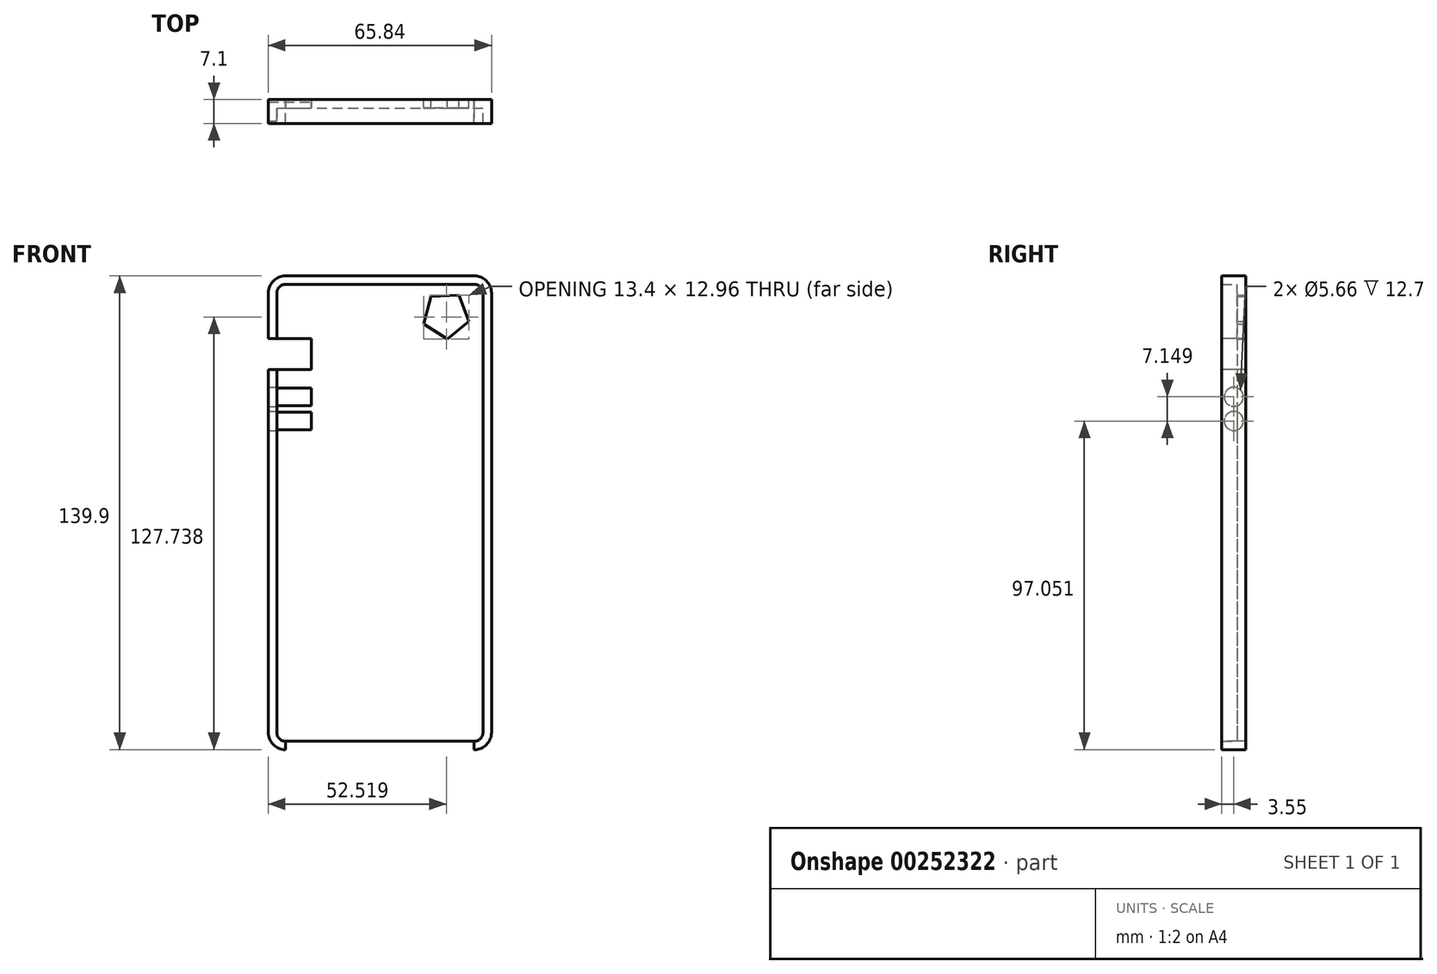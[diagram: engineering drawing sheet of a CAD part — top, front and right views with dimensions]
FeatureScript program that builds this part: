
annotation { "Feature Type Name" : "Feature", "Feature Type Description" : "" }
export const myFeature = defineFeature(function(context is Context, id is Id, definition is map)
    precondition{}
    {
        {
            var Q0;
            Q0=qCreatedBy(makeId("Front.planeOp"),FACE);
            var sketch = newSketch(context, id + "F0", { "sketchPlane" : qUnion([Q0])});
            skLineSegment(sketch, "E0.bottom", {"start": v(32.92, 69.95) * mm, "end": v(-32.92, 69.95) * mm});
            skLineSegment(sketch, "E0.top", {"start": v(32.92, -69.95) * mm, "end": v(-32.92, -69.95) * mm});
            skLineSegment(sketch, "E0.left", {"start": v(32.92, 69.95) * mm, "end": v(32.92, -69.95) * mm});
            skLineSegment(sketch, "E0.right", {"start": v(-32.92, 69.95) * mm, "end": v(-32.92, -69.95) * mm});
            skPoint(sketch, "E0.middle", {"position": v(0, 0) * mm});
            skSolve(sketch);
        }
        {
            var Q0;
            Q0=makeQuery(id+"F0.imprint","IMPRINT",FACE,{"disambiguationData":[TD([[makeQuery(id+"F0.imprint","IMPRINT",EDGE,{"derivedFrom":sQuery(id+"F0.wireOp",EDGE,"E0.bottom")}),1.0]])]});
            extrude(context, id + "F1", {"entities" : qUnion([Q0]), "endBound" : BoundingType.SYMMETRIC, "depth" : 7.1 * mm});
        }
        {
            var Q0;
            Q0=makeQuery(id+"F1.opExtrude","SWEPT_EDGE",EDGE,{"disambiguationData":[OSD([sQuery(id+"F0.wireOp",EDGE,"E0.bottom"),sQuery(id+"F0.wireOp",EDGE,"E0.right")])]});
            var Q1;
            Q1=makeQuery(id+"F1.opExtrude","SWEPT_EDGE",EDGE,{"disambiguationData":[OSD([sQuery(id+"F0.wireOp",EDGE,"E0.bottom"),sQuery(id+"F0.wireOp",EDGE,"E0.left")])]});
            var Q2;
            Q2=makeQuery(id+"F1.opExtrude","SWEPT_EDGE",EDGE,{"disambiguationData":[OSD([sQuery(id+"F0.wireOp",EDGE,"E0.top"),sQuery(id+"F0.wireOp",EDGE,"E0.right")])]});
            var Q3;
            Q3=makeQuery(id+"F1.opExtrude","SWEPT_EDGE",EDGE,{"disambiguationData":[OSD([sQuery(id+"F0.wireOp",EDGE,"E0.top"),sQuery(id+"F0.wireOp",EDGE,"E0.left")])]});
            fillet(context, id + "F2", {"entities" : qUnion([Q0, Q1, Q2, Q3]), "radius" : 5.08 * mm, "tangentPropagation" : true, "allowEdgeOverflow" : false});
        }
        {
            var Q0;
            Q0=makeQuery(id+"F1.opExtrude","CAP_FACE",FACE,{"disambiguationData":[OSD([sQuery(id+"F0.wireOp",EDGE,"E0.bottom"),sQuery(id+"F0.wireOp",EDGE,"E0.top"),sQuery(id+"F0.wireOp",EDGE,"E0.left"),sQuery(id+"F0.wireOp",EDGE,"E0.right")])],"isStart":false});
            shell(context, id + "F3", {"entities" : qUnion([Q0]), "thickness" : 2.5 * mm});
        }
        {
            var Q0;
            Q0=qCreatedBy(makeId("Front.planeOp"),FACE);
            var sketch = newSketch(context, id + "F4", { "sketchPlane" : qUnion([Q0])});
            skCircle(sketch, "E1.cCircle", {"center": v(19.48, 58.35) * mm, "radius": 5.7 * mm, "construction": true});
            skLineSegment(sketch, "E1.0", {"start": v(19.86, 51.3) * mm, "end": v(12.9, 55.81) * mm});
            skLineSegment(sketch, "E1.1", {"start": v(12.9, 55.81) * mm, "end": v(15.04, 63.83) * mm});
            skLineSegment(sketch, "E1.2", {"start": v(15.04, 63.83) * mm, "end": v(23.32, 64.27) * mm});
            skLineSegment(sketch, "E1.3", {"start": v(23.32, 64.27) * mm, "end": v(26.3, 56.53) * mm});
            skLineSegment(sketch, "E1.4", {"start": v(26.3, 56.53) * mm, "end": v(19.86, 51.3) * mm});
            skPoint(sketch, "E1.0.midPoint", {"position": v(16.38, 53.56) * mm});
            skSolve(sketch);
        }
        {
            var Q0;
            Q0=makeQuery(id+"F4.imprint","IMPRINT",FACE,{"disambiguationData":[TD([[makeQuery(id+"F4.imprint","IMPRINT",EDGE,{"derivedFrom":sQuery(id+"F4.wireOp",EDGE,"E1.0")}),-1.0]])]});
            extrude(context, id + "F5", {"entities" : qUnion([Q0]), "operationType" : NewBodyOperationType.REMOVE, "endBound" : BoundingType.SYMMETRIC, "depth" : 25.4 * mm});
        }
        {
            var Q0;
            Q0=makeQuery(id+"F1.opExtrude","SWEPT_FACE",FACE,{"disambiguationData":[OSD([sQuery(id+"F0.wireOp",EDGE,"E0.top")])]});
            var sketch = newSketch(context, id + "F6", { "sketchPlane" : qUnion([Q0])});
            skLineSegment(sketch, "E2.bottom", {"start": v(-27.84, 3.55) * mm, "end": v(27.84, 3.55) * mm});
            skLineSegment(sketch, "E2.top", {"start": v(-27.84, -3.55) * mm, "end": v(27.84, -3.55) * mm});
            skLineSegment(sketch, "E2.left", {"start": v(-27.84, 3.55) * mm, "end": v(-27.84, -3.55) * mm});
            skLineSegment(sketch, "E2.right", {"start": v(27.84, 3.55) * mm, "end": v(27.84, -3.55) * mm});
            skSolve(sketch);
        }
        {
            var Q0;
            Q0 = qSketchRegion(id + "F6", true);
            extrude(context, id + "F7", {"entities" : qUnion([Q0]), "operationType" : NewBodyOperationType.REMOVE, "endBound" : BoundingType.SYMMETRIC, "depth" : 5 * mm});
        }
        {
            var Q0;
            Q0=makeQuery(id+"F1.opExtrude","SWEPT_FACE",FACE,{"disambiguationData":[OSD([sQuery(id+"F0.wireOp",EDGE,"E0.right")])]});
            var sketch = newSketch(context, id + "F8", { "sketchPlane" : qUnion([Q0])});
            skLineSegment(sketch, "E3.bottom", {"start": v(-3.55, 51.4) * mm, "end": v(3.55, 51.4) * mm});
            skLineSegment(sketch, "E3.top", {"start": v(-3.55, 42.36) * mm, "end": v(3.55, 42.36) * mm});
            skLineSegment(sketch, "E3.left", {"start": v(-3.55, 51.4) * mm, "end": v(-3.55, 42.36) * mm});
            skLineSegment(sketch, "E3.right", {"start": v(3.55, 51.4) * mm, "end": v(3.55, 42.36) * mm});
            skCircle(sketch, "E4", {"center": v(0, 34.25) * mm, "radius": 2.83 * mm});
            skCircle(sketch, "E5", {"center": v(0, 27.1) * mm, "radius": 2.83 * mm});
            skSolve(sketch);
        }
        {
            var Q0;
            Q0=makeQuery(id+"F8.imprint","IMPRINT",FACE,{"disambiguationData":[TD([[makeQuery(id+"F8.imprint","IMPRINT",EDGE,{"derivedFrom":sQuery(id+"F8.wireOp",EDGE,"E5")}),1.0]])]});
            var Q1;
            {var subQ0=sQuery(id+"F8.wireOp",EDGE,"E4");var subQ1=makeQuery(id+"F1.opExtrude","CAP_EDGE",EDGE,{"disambiguationData":[OSD([sQuery(id+"F0.wireOp",EDGE,"E0.right")])],"isStart":true});var subQ2=makeQuery(id+"F8.imprint","INTERSECT",VERTEX,{"disambiguationData":[OD(0.0)],"derivedFrom":[subQ1,subQ0]});Q1=makeQuery(id+"F8.imprint","IMPRINT",FACE,{"disambiguationData":[TD([[makeQuery(id+"F8.imprint","IMPRINT",EDGE,{"disambiguationData":[TD([[subQ2,-1.0]])],"derivedFrom":subQ0}),1.0]])]});}
            var Q2;
            {var subQ0=sQuery(id+"F8.wireOp",EDGE,"E4");var subQ1=makeQuery(id+"F1.opExtrude","CAP_EDGE",EDGE,{"disambiguationData":[OSD([sQuery(id+"F0.wireOp",EDGE,"E0.right")])],"isStart":false});var subQ2=makeQuery(id+"F8.imprint","INTERSECT",VERTEX,{"disambiguationData":[OD(0.0)],"derivedFrom":[subQ1,subQ0]});Q2=makeQuery(id+"F8.imprint","IMPRINT",FACE,{"disambiguationData":[TD([[makeQuery(id+"F8.imprint","IMPRINT",EDGE,{"disambiguationData":[TD([[subQ2,1.0]])],"derivedFrom":subQ0}),1.0]])]});}
            var Q3;
            {var subQ0=sQuery(id+"F8.wireOp",EDGE,"E4");var subQ1=sQuery(id+"F0.wireOp",EDGE,"E0.right");var subQ2=makeQuery(id+"F1.opExtrude","CAP_EDGE",EDGE,{"disambiguationData":[OSD([subQ1])],"isStart":true});var subQ3=makeQuery(id+"F8.imprint","INTERSECT",VERTEX,{"disambiguationData":[OD(0.0)],"derivedFrom":[subQ2,subQ0]});Q3=makeQuery(id+"F8.imprint","IMPRINT",FACE,{"disambiguationData":[TD([[makeQuery(id+"F8.imprint","IMPRINT",EDGE,{"disambiguationData":[TD([[subQ3,1.0]])],"derivedFrom":subQ0}),1.0]])]});}
            var Q4;
            Q4=makeQuery(id+"F8.imprint","IMPRINT",FACE,{"disambiguationData":[TD([[makeQuery(id+"F8.imprint","IMPRINT",EDGE,{"derivedFrom":sQuery(id+"F8.wireOp",EDGE,"E3.bottom")}),-1.0]])]});
            extrude(context, id + "F9", {"entities" : qUnion([Q0, Q1, Q2, Q3, Q4]), "operationType" : NewBodyOperationType.REMOVE, "endBound" : BoundingType.SYMMETRIC, "depth" : 25.4 * mm});
        }
        {
            var Q0;
            Q0 = qSketchRegion(id + "F8", true);
            extrude(context, id + "F10", {"entities" : qUnion([Q0]), "operationType" : NewBodyOperationType.REMOVE, "endBound" : BoundingType.SYMMETRIC, "depth" : 1 * mm});
        }
    });
